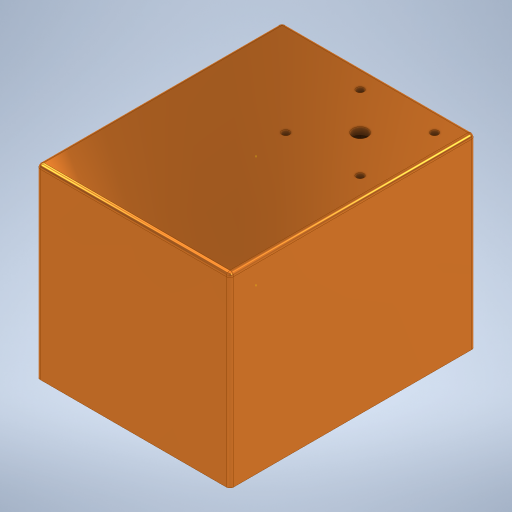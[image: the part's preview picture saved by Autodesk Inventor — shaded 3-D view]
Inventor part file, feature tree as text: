
AUTODESK INVENTOR PART (.ipt)
format: ipt  version: 2023 (Build 270158000, 158)  size: 380,928 bytes
history: native  units: mm
features: extrude x13, sketch x13, fillet x3, chamfer x1, projected_geometry x1
ambient origin geometry x8: Origin, YZ Plane, XZ Plane, XY Plane, X Axis, Y Axis, Z Axis, Center Point
bodies: Solid1 (feature_tree)
feature tree (31):
  extrude  "Extrusion1"  Depth=330.0mm
  extrude  "Extrusion2"  Depth=10.0mm
  fillet  "Fillet1"  Radius=10.0mm
  extrude  "Extrusion3"  Depth=5.0mm
  extrude  "Extrusion4"  Depth=10.0mm
  extrude  "Extrusion5"  Depth=10.0mm
  extrude  "Extrusion6"  Depth=22.5mm
  sketch  "Sketch8"  dims[d14=100.0mm d15=22.5mm]
  extrude  "Extrusion7"  Depth=8.0mm TaperAngle=0.0deg
  fillet  "Fillet2"  Radius=20.0mm
  sketch  "Sketch10"  dims[d16=22.5mm d17=8.0mm d18=0.0mm d19=20.0mm]
  extrude  "Extrusion8"  Depth=50.0mm
  extrude  "Extrusion9"  Depth=70.0mm
  extrude  "Extrusion11"  Depth=150.0mm TaperAngle=0.0deg
  extrude  "Extrusion12"  Depth=35.0mm
  chamfer  "Chamfer2"  Distance=150.0mm
  extrude  "Extrusion13"  Depth=5.0mm
  extrude  "Extrusion14"  Depth=15.0mm
  fillet  "Fillet3"  Radius=14.5mm
  sketch  "Sketch1"  dims[d0=260.0mm d1=330.0mm]
  sketch  "Sketch2"  dims[d2=250.0mm d3=0.0mm d4=10.0mm d5=10.0mm]
  sketch  "Sketch3"  dims[d6=240.0mm d7=0.0mm d8=5.0mm]
  sketch  "Sketch4"  dims[d9=10.0mm d10=10.0mm]
  sketch  "Sketch7"  dims[d11=10.0mm d12=10.0mm d13=100.0mm]
  sketch  "Sketch11"  dims[d20=50.0mm d21=50.0mm]
  sketch  "Sketch12"  dims[d22=8.0mm d23=0.0mm d24=70.0mm]
  sketch  "Sketch15"  dims[d25=60.0mm d26=150.0mm d27=0.0mm]
  sketch  "Sketch17"  dims[d28=65.0mm d29=35.0mm d30=150.0mm d31=0.0mm]
  sketch  "Sketch18"  dims[d32=5.0mm d33=5.0mm]
  sketch  "Sketch19"  dims[d39=150.0mm d40=0.0mm d43=14.5mm d44=14.5mm d45=15.0mm d46=1.0mm d47=1.0mm d48=1.0mm d49=1.0mm d50=5.0mm d51=0.0mm d52=70.0mm d53=150.0mm d54=60.0mm d55=130.0mm d56=0.0mm d57=0.0mm d68=50.0mm d69=0.0mm d70=0.5mm d71=0.5mm d72=0.5mm d73=0.5mm d74=5.0mm d75=0.0mm d76=0.2mm d77=2.0mm d78=45.0deg d79=100.0mm d80=30.0mm d82=150.0mm d83=0.0mm d84=5.0mm d85=5.0mm d87=5.0mm d88=140.0mm d89=0.0mm d90=2.0mm d91=15.0mm]
  projected_geometry  "Projected Loop1"
